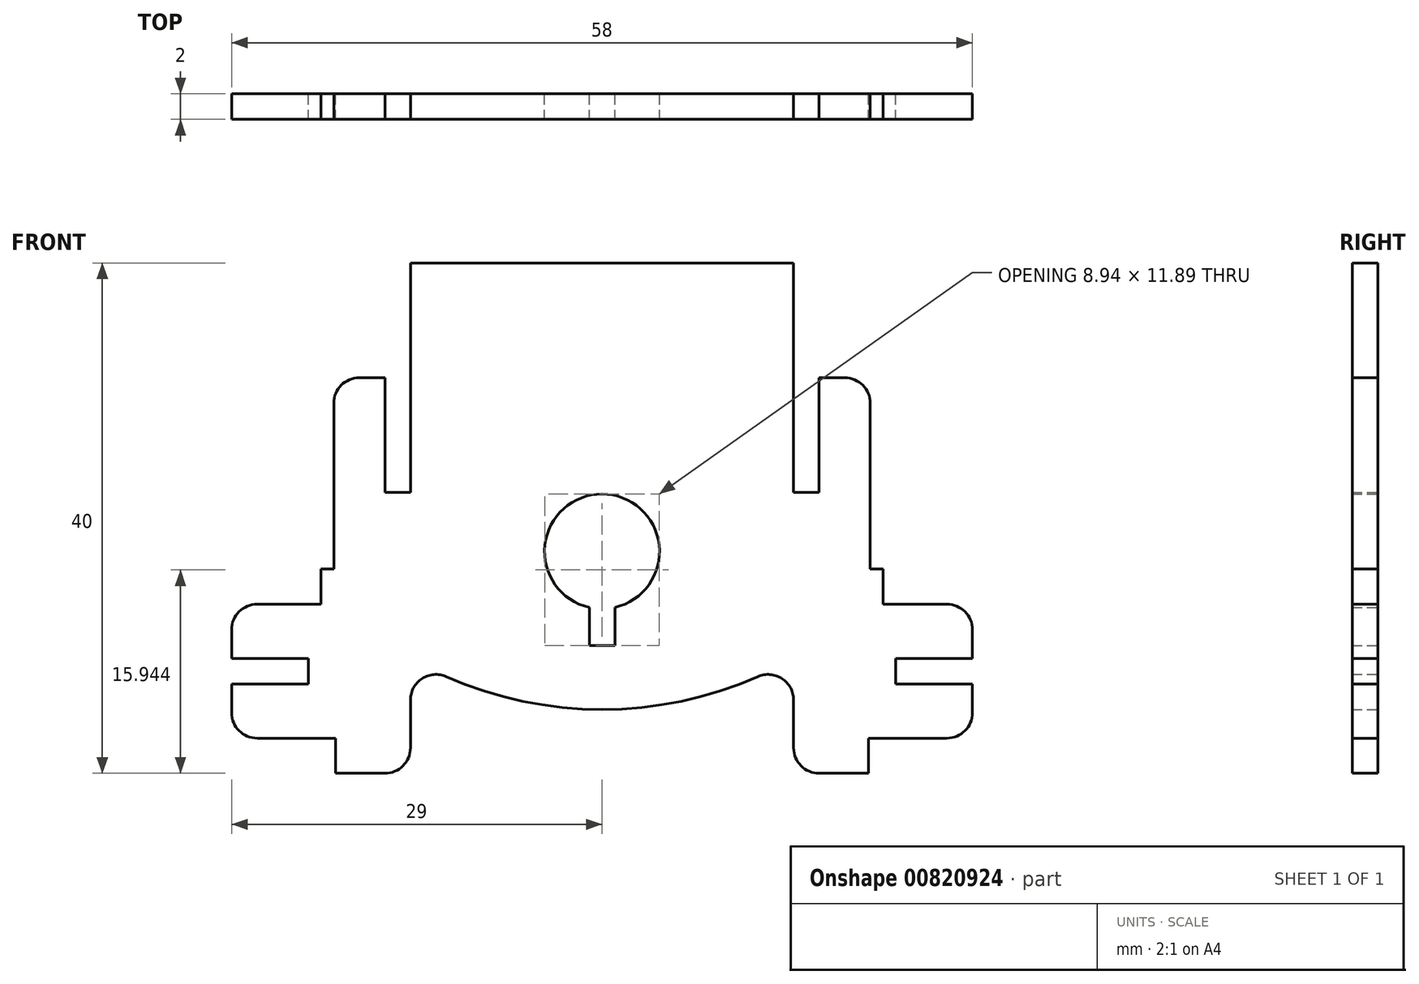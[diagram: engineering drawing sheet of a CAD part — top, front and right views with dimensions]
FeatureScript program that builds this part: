
annotation { "Feature Type Name" : "Feature", "Feature Type Description" : "" }
export const myFeature = defineFeature(function(context is Context, id is Id, definition is map)
    precondition{}
    {
        {
            var Q0;
            Q0=qCreatedBy(makeId("Front.planeOp"),FACE);
            var sketch = newSketch(context, id + "F0", { "sketchPlane" : qUnion([Q0])});
            skLineSegment(sketch, "E0.bottom", {"start": v(-15, 15.5) * mm, "end": v(15, 15.5) * mm});
            skLineSegment(sketch, "E0.left", {"start": v(-15, 15.5) * mm, "end": v(-15, -2.5) * mm});
            skLineSegment(sketch, "E0.right", {"start": v(15, 15.5) * mm, "end": v(15, -2.5) * mm});
            skPoint(sketch, "E0.middle", {"position": v(0, 0) * mm});
            skPoint(sketch, "E1", {"position": v(0, -19.5) * mm});
            skPoint(sketch, "E1.positionSnap0", {"position": v(0, -15.5) * mm});
            skArc(sketch, "E2", {"start": v(-12.2, -16.92) * mm, "mid": v(0, -19.5) * mm, "end": v(12.2, -16.92) * mm});
            skLineSegment(sketch, "E3", {"start": v(-1, -14.5) * mm, "end": v(1, -14.5) * mm});
            skLineSegment(sketch, "E4", {"start": v(-1, -14.5) * mm, "end": v(-1, -11.5) * mm});
            skLineSegment(sketch, "E5", {"start": v(1, -14.5) * mm, "end": v(1, -11.5) * mm});
            skArc(sketch, "E6", {"start": v(1, -11.5) * mm, "mid": v(0, -2.61) * mm, "end": v(-1, -11.5) * mm});
            skLineSegment(sketch, "E7", {"start": v(-15, -2.5) * mm, "end": v(-17, -2.5) * mm});
            skLineSegment(sketch, "E8", {"start": v(-17, -2.5) * mm, "end": v(-17, 6.5) * mm});
            skLineSegment(sketch, "E9", {"start": v(-17, 6.5) * mm, "end": v(-19, 6.5) * mm});
            skLineSegment(sketch, "E10", {"start": v(-20.87, -24.5) * mm, "end": v(-17, -24.5) * mm});
            skLineSegment(sketch, "E11", {"start": v(-21, 4.5) * mm, "end": v(-21, -8.5) * mm});
            skLineSegment(sketch, "E12", {"start": v(-21, -8.5) * mm, "end": v(-22, -8.5) * mm});
            skLineSegment(sketch, "E13", {"start": v(-20.87, -24.5) * mm, "end": v(-20.87, -21.75) * mm});
            skLineSegment(sketch, "E14.bottom", {"start": v(-27, -11.25) * mm, "end": v(-22, -11.25) * mm});
            skLineSegment(sketch, "E14.top", {"start": v(-27, -21.75) * mm, "end": v(-20.87, -21.75) * mm});
            skLineSegment(sketch, "E14.left", {"start": v(-29, -13.25) * mm, "end": v(-29, -15.5) * mm});
            skPoint(sketch, "E14.middle", {"position": v(-20.87, -16.5) * mm});
            skLineSegment(sketch, "E15", {"start": v(-22, -8.5) * mm, "end": v(-22, -11.25) * mm});
            skLineSegment(sketch, "E16", {"start": v(-15, -22.5) * mm, "end": v(-15, -18.75) * mm});
            skPoint(sketch, "E16.startSnap0", {"position": v(-10.44, -24.5) * mm});
            skPoint(sketch, "E17.trimOffspring.end.orphan", {"position": v(-12.75, -21.75) * mm});
            skPoint(sketch, "E18.trimOffspring.end.orphan", {"position": v(-12.75, -11.25) * mm});
            skPoint(sketch, "E19.trimOffspring.end.orphan", {"position": v(-20.87, -8.5) * mm});
            skLineSegment(sketch, "E20", {"start": v(-29, -15.5) * mm, "end": v(-23, -15.5) * mm});
            skLineSegment(sketch, "E21", {"start": v(-29, -17.5) * mm, "end": v(-23, -17.5) * mm});
            skLineSegment(sketch, "E22", {"start": v(-23, -17.5) * mm, "end": v(-23, -15.5) * mm});
            skLineSegment(sketch, "E23.trimOffspring", {"start": v(-29, -17.5) * mm, "end": v(-29, -19.75) * mm});
            skPoint(sketch, "E24.newPointA", {"position": v(0, -24.5) * mm});
            skPoint(sketch, "E24.newPointB", {"position": v(-15, -24.5) * mm});
            skArc(sketch, "E24.filletArc", {"start": v(-17, -24.5) * mm, "mid": v(-15.59, -23.91) * mm, "end": v(-15, -22.5) * mm});
            skPoint(sketch, "E25.visualSharp", {"position": v(-15, -15.5) * mm});
            skArc(sketch, "E25.filletArc", {"start": v(-12.2, -16.92) * mm, "mid": v(-14.1, -17.08) * mm, "end": v(-15, -18.75) * mm});
            skPoint(sketch, "E26.visualSharp", {"position": v(-21, 6.5) * mm});
            skArc(sketch, "E26.filletArc", {"start": v(-19, 6.5) * mm, "mid": v(-20.41, 5.91) * mm, "end": v(-21, 4.5) * mm});
            skPoint(sketch, "E27.visualSharp", {"position": v(-29, -11.25) * mm});
            skArc(sketch, "E27.filletArc", {"start": v(-27, -11.25) * mm, "mid": v(-28.41, -11.84) * mm, "end": v(-29, -13.25) * mm});
            skPoint(sketch, "E28.visualSharp", {"position": v(-29, -21.75) * mm});
            skArc(sketch, "E28.filletArc", {"start": v(-29, -19.75) * mm, "mid": v(-28.41, -21.16) * mm, "end": v(-27, -21.75) * mm});
            skLineSegment(sketch, "E29.MirrorCS", {"start": v(15, -2.5) * mm, "end": v(17, -2.5) * mm});
            skLineSegment(sketch, "E30.MirrorCS", {"start": v(17, -2.5) * mm, "end": v(17, 6.5) * mm});
            skLineSegment(sketch, "E31.MirrorCS", {"start": v(17, 6.5) * mm, "end": v(19, 6.5) * mm});
            skArc(sketch, "E32.MirrorCS", {"start": v(19, 6.5) * mm, "mid": v(20.41, 5.91) * mm, "end": v(21, 4.5) * mm});
            skLineSegment(sketch, "E33.MirrorCS", {"start": v(21, 4.5) * mm, "end": v(21, -8.5) * mm});
            skLineSegment(sketch, "E34.MirrorCS", {"start": v(21, -8.5) * mm, "end": v(22, -8.5) * mm});
            skLineSegment(sketch, "E35.MirrorCS", {"start": v(22, -8.5) * mm, "end": v(22, -11.25) * mm});
            skLineSegment(sketch, "E36.MirrorCS", {"start": v(27, -11.25) * mm, "end": v(22, -11.25) * mm});
            skArc(sketch, "E37.MirrorCS", {"start": v(27, -11.25) * mm, "mid": v(28.41, -11.84) * mm, "end": v(29, -13.25) * mm});
            skLineSegment(sketch, "E38.MirrorCS", {"start": v(29, -13.25) * mm, "end": v(29, -15.5) * mm});
            skLineSegment(sketch, "E39.MirrorCS", {"start": v(29, -15.5) * mm, "end": v(23, -15.5) * mm});
            skLineSegment(sketch, "E40.MirrorCS", {"start": v(23, -17.5) * mm, "end": v(23, -15.5) * mm});
            skLineSegment(sketch, "E41.MirrorCS", {"start": v(29, -17.5) * mm, "end": v(23, -17.5) * mm});
            skLineSegment(sketch, "E42.MirrorCS", {"start": v(29, -17.5) * mm, "end": v(29, -19.75) * mm});
            skArc(sketch, "E43.MirrorCS", {"start": v(29, -19.75) * mm, "mid": v(28.41, -21.16) * mm, "end": v(27, -21.75) * mm});
            skLineSegment(sketch, "E44.MirrorCS", {"start": v(27, -21.75) * mm, "end": v(20.87, -21.75) * mm});
            skLineSegment(sketch, "E45.MirrorCS", {"start": v(20.87, -24.5) * mm, "end": v(20.87, -21.75) * mm});
            skLineSegment(sketch, "E46.MirrorCS", {"start": v(20.87, -24.5) * mm, "end": v(17, -24.5) * mm});
            skArc(sketch, "E47.MirrorCS", {"start": v(17, -24.5) * mm, "mid": v(15.59, -23.91) * mm, "end": v(15, -22.5) * mm});
            skLineSegment(sketch, "E48.MirrorCS", {"start": v(15, -22.5) * mm, "end": v(15, -18.75) * mm});
            skArc(sketch, "E49.MirrorCS", {"start": v(12.2, -16.92) * mm, "mid": v(14.1, -17.08) * mm, "end": v(15, -18.75) * mm});
            skPoint(sketch, "E50.orphan", {"position": v(15, -15.5) * mm});
            skLineSegment(sketch, "E51.trimOffspring", {"start": v(0, -14.5) * mm, "end": v(0, -19.5) * mm});
            skPoint(sketch, "E52.start.orphan", {"position": v(0, 15.5) * mm});
            skSolve(sketch);
        }
        {
            var Q0;
            Q0 = qSketchRegion(id + "F0", true);
            extrude(context, id + "F1", {"entities" : qUnion([Q0]), "depth" : 2 * mm, "offsetDistance" : 25 * mm});
        }
    });
